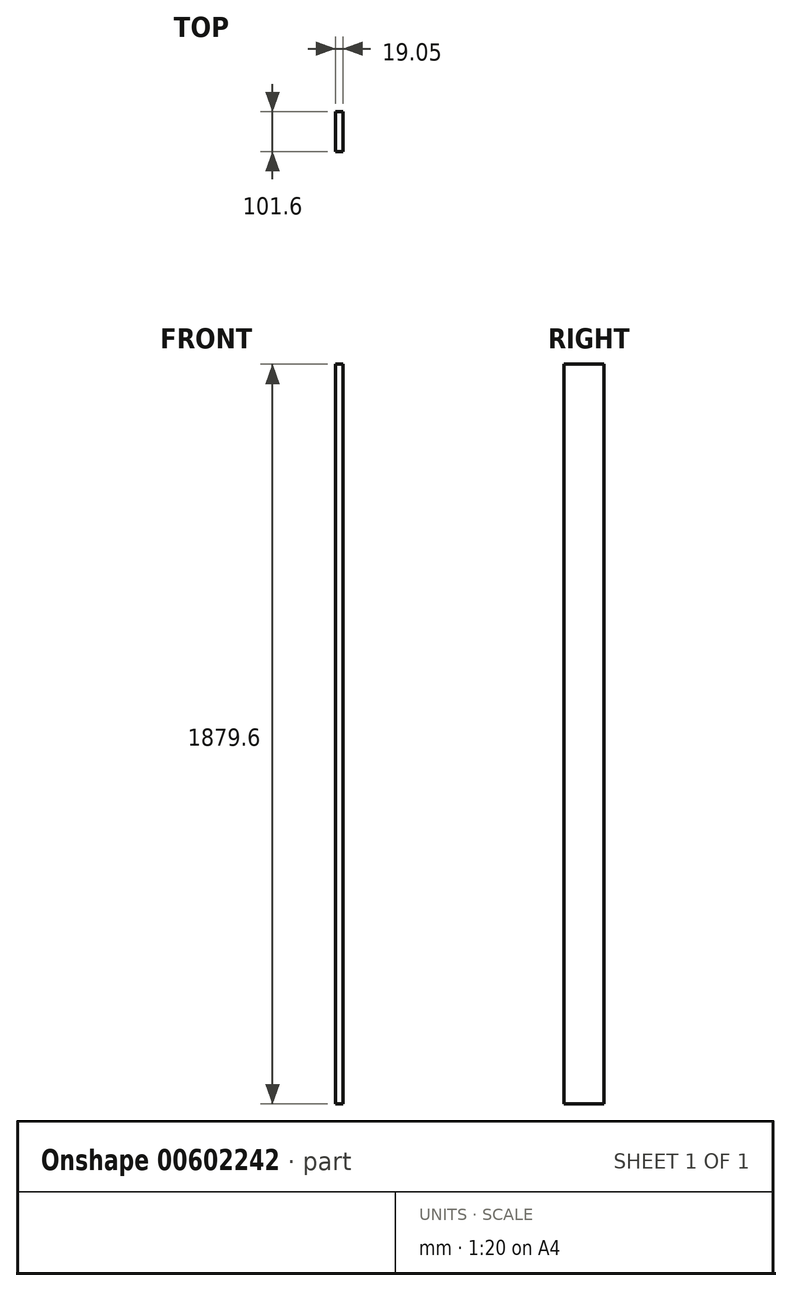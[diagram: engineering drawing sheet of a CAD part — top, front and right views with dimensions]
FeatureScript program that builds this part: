
annotation { "Feature Type Name" : "Feature", "Feature Type Description" : "" }
export const myFeature = defineFeature(function(context is Context, id is Id, definition is map)
    precondition{}
    {
        {
            var Q0;
            Q0=qCreatedBy(makeId("Right.planeOp"),FACE);
            var sketch = newSketch(context, id + "F0", { "sketchPlane" : qUnion([Q0])});
            skLineSegment(sketch, "E0.right", {"start": v(-50.8, -939.8) * mm, "end": v(-50.8, 939.8) * mm});
            skLineSegment(sketch, "E1", {"start": v(50.8, 939.8) * mm, "end": v(-50.8, 939.8) * mm});
            skLineSegment(sketch, "E2", {"start": v(50.8, -939.8) * mm, "end": v(-50.8, -939.8) * mm});
            skLineSegment(sketch, "E3", {"start": v(50.8, 939.8) * mm, "end": v(50.8, -939.8) * mm});
            skSolve(sketch);
        }
        {
            var Q0;
            Q0 = qSketchRegion(id + "F0", true);
            extrude(context, id + "F1", {"entities" : qUnion([Q0]), "depth" : 19.05 * mm, "offsetDistance" : 25.4 * mm});
        }
    });
